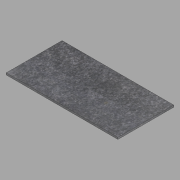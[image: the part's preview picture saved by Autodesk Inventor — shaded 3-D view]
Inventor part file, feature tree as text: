
AUTODESK INVENTOR PART (.ipt)
format: ipt  version: 2022.2 (Build 262287000, 287)  size: 107,008 bytes
history: native  units: in
note: dims shown in document units (in); Inventor stores cm internally (conversion verified against a paired STEP export)
features: extrude x1, sketch x1
ambient origin geometry x8: Origin, YZ Plane, XZ Plane, XY Plane, X Axis, Y Axis, Z Axis, Center Point
bodies: Solid1 (feature_tree)
feature tree (2):
  extrude  "Extrusion1"  Depth=30.0in
  sketch  "Sketch1"  dims[d0=60.0in d1=30.0in d2=1.0in d3=0.0in]
